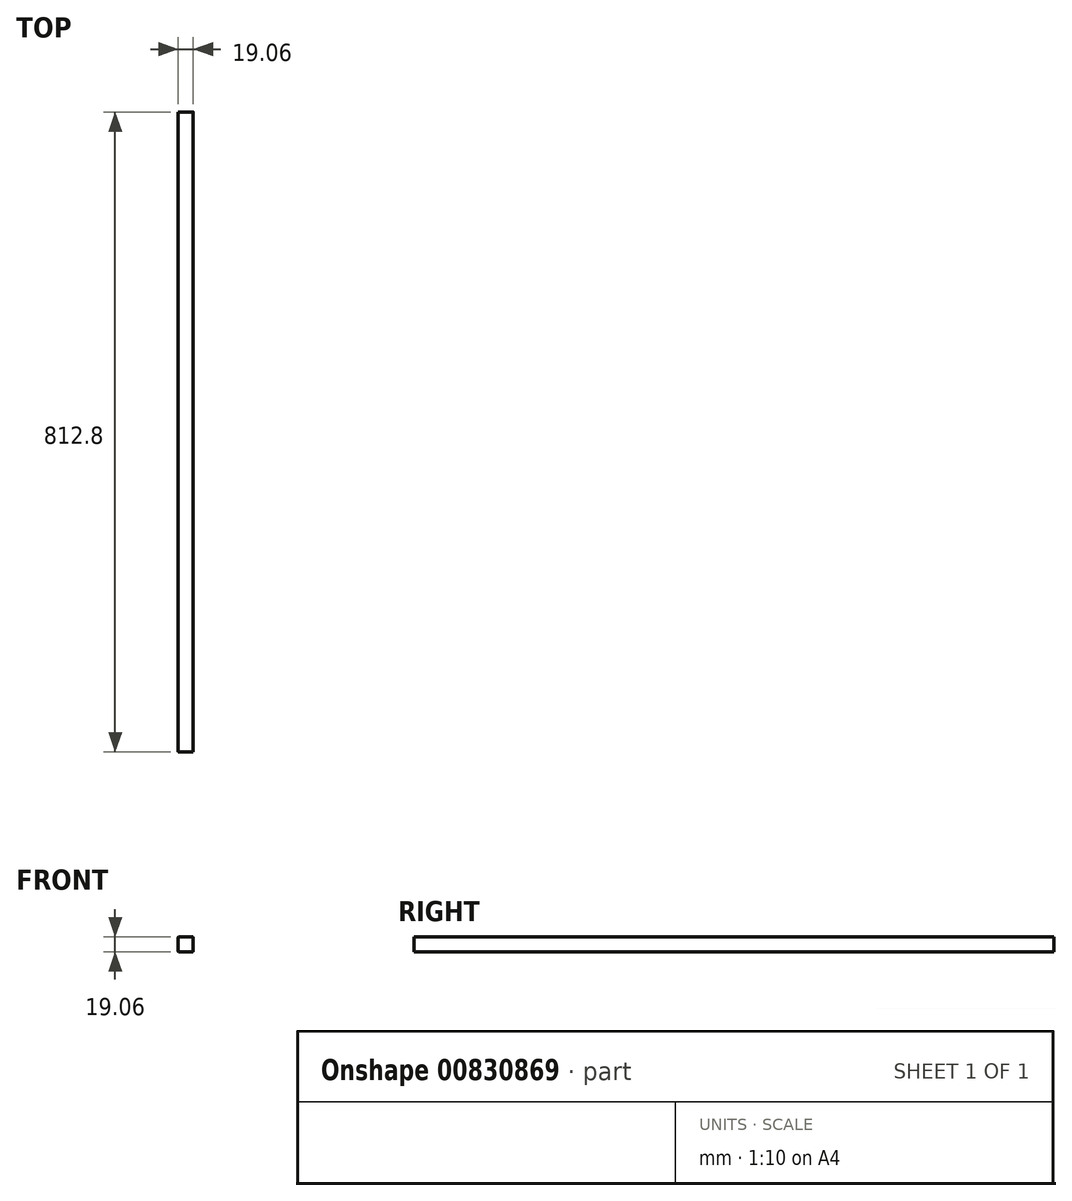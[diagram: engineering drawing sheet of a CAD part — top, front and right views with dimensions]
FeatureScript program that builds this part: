
annotation { "Feature Type Name" : "Feature", "Feature Type Description" : "" }
export const myFeature = defineFeature(function(context is Context, id is Id, definition is map)
    precondition{}
    {
        {
            var Q0;
            Q0=qCreatedBy(makeId("Front.planeOp"),FACE);
            var sketch = newSketch(context, id + "F0", { "sketchPlane" : qUnion([Q0])});
            skLineSegment(sketch, "E0.bottom", {"start": v(-8.76, 9.53) * mm, "end": v(8.76, 9.53) * mm});
            skLineSegment(sketch, "E0.top", {"start": v(-8.76, -9.53) * mm, "end": v(8.76, -9.53) * mm});
            skLineSegment(sketch, "E0.left", {"start": v(-9.53, 8.76) * mm, "end": v(-9.53, -8.76) * mm});
            skLineSegment(sketch, "E0.right", {"start": v(9.53, 8.76) * mm, "end": v(9.53, -8.76) * mm});
            skPoint(sketch, "E0.middle", {"position": v(0, 0) * mm});
            skPoint(sketch, "E1.visualSharp", {"position": v(-9.52, 9.53) * mm});
            skArc(sketch, "E1.filletArc", {"start": v(-8.76, 9.53) * mm, "mid": v(-9.3, 9.3) * mm, "end": v(-9.53, 8.76) * mm});
            skPoint(sketch, "E2.visualSharp", {"position": v(9.53, 9.53) * mm});
            skArc(sketch, "E2.filletArc", {"start": v(9.53, 8.76) * mm, "mid": v(9.3, 9.3) * mm, "end": v(8.76, 9.53) * mm});
            skPoint(sketch, "E3.visualSharp", {"position": v(9.53, -9.53) * mm});
            skArc(sketch, "E3.filletArc", {"start": v(8.76, -9.53) * mm, "mid": v(9.3, -9.3) * mm, "end": v(9.53, -8.76) * mm});
            skPoint(sketch, "E4.visualSharp", {"position": v(-9.53, -9.53) * mm});
            skArc(sketch, "E4.filletArc", {"start": v(-9.53, -8.76) * mm, "mid": v(-9.3, -9.3) * mm, "end": v(-8.76, -9.53) * mm});
            skSolve(sketch);
        }
        {
            var Q0;
            Q0=makeQuery(id+"F0.imprint","IMPRINT",FACE,{"disambiguationData":[TD([[makeQuery(id+"F0.imprint","IMPRINT",EDGE,{"derivedFrom":sQuery(id+"F0.wireOp",EDGE,"E0.bottom")}),-1.0]])]});
            extrude(context, id + "F1", {"entities" : qUnion([Q0]), "endBound" : BoundingType.SYMMETRIC, "depth" : 812.8 * mm, "offsetDistance" : 25.4 * mm});
        }
    });
